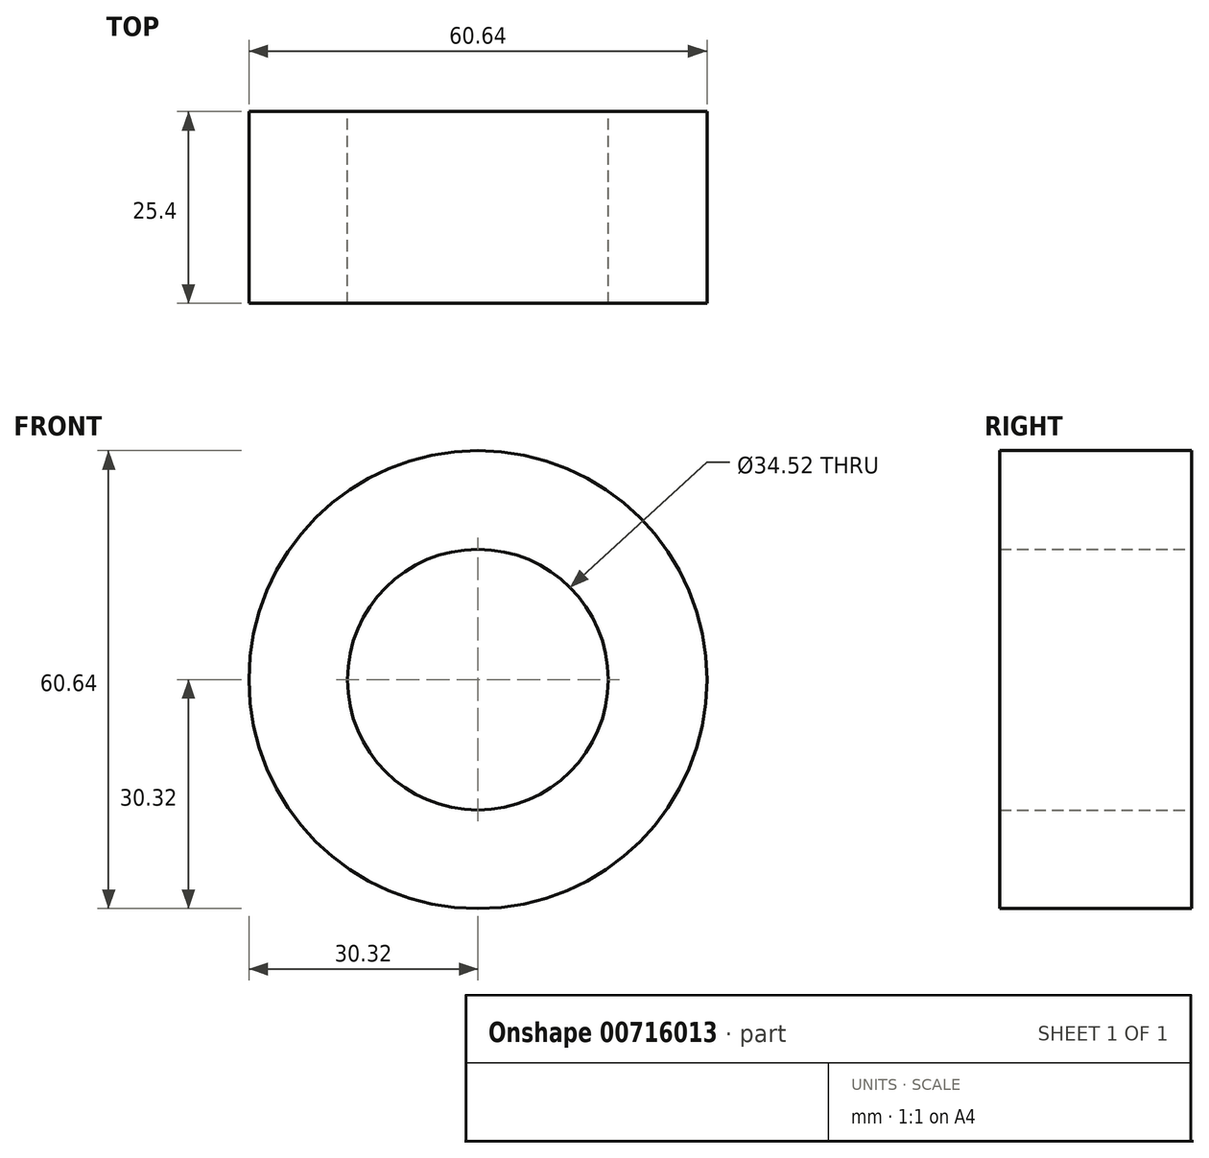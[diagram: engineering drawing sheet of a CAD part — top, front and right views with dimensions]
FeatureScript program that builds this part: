
annotation { "Feature Type Name" : "Feature", "Feature Type Description" : "" }
export const myFeature = defineFeature(function(context is Context, id is Id, definition is map)
    precondition{}
    {
        {
            var Q0;
            Q0=qCreatedBy(makeId("Front.planeOp"),FACE);
            var sketch = newSketch(context, id + "F0", { "sketchPlane" : qUnion([Q0])});
            skCircle(sketch, "E0", {"center": v(0, 0) * mm, "radius": 17.26 * mm});
            skCircle(sketch, "E1", {"center": v(0, 0) * mm, "radius": 30.32 * mm});
            skSolve(sketch);
        }
        {
            var Q0;
            Q0=makeQuery(id+"F0.imprint","IMPRINT",FACE,{"disambiguationData":[TD([[makeQuery(id+"F0.imprint","IMPRINT",EDGE,{"derivedFrom":sQuery(id+"F0.wireOp",EDGE,"E0")}),-1.0]])]});
            extrude(context, id + "F1", {"entities" : qUnion([Q0]), "depth" : 25.4 * mm, "offsetDistance" : 25.4 * mm});
        }
    });
